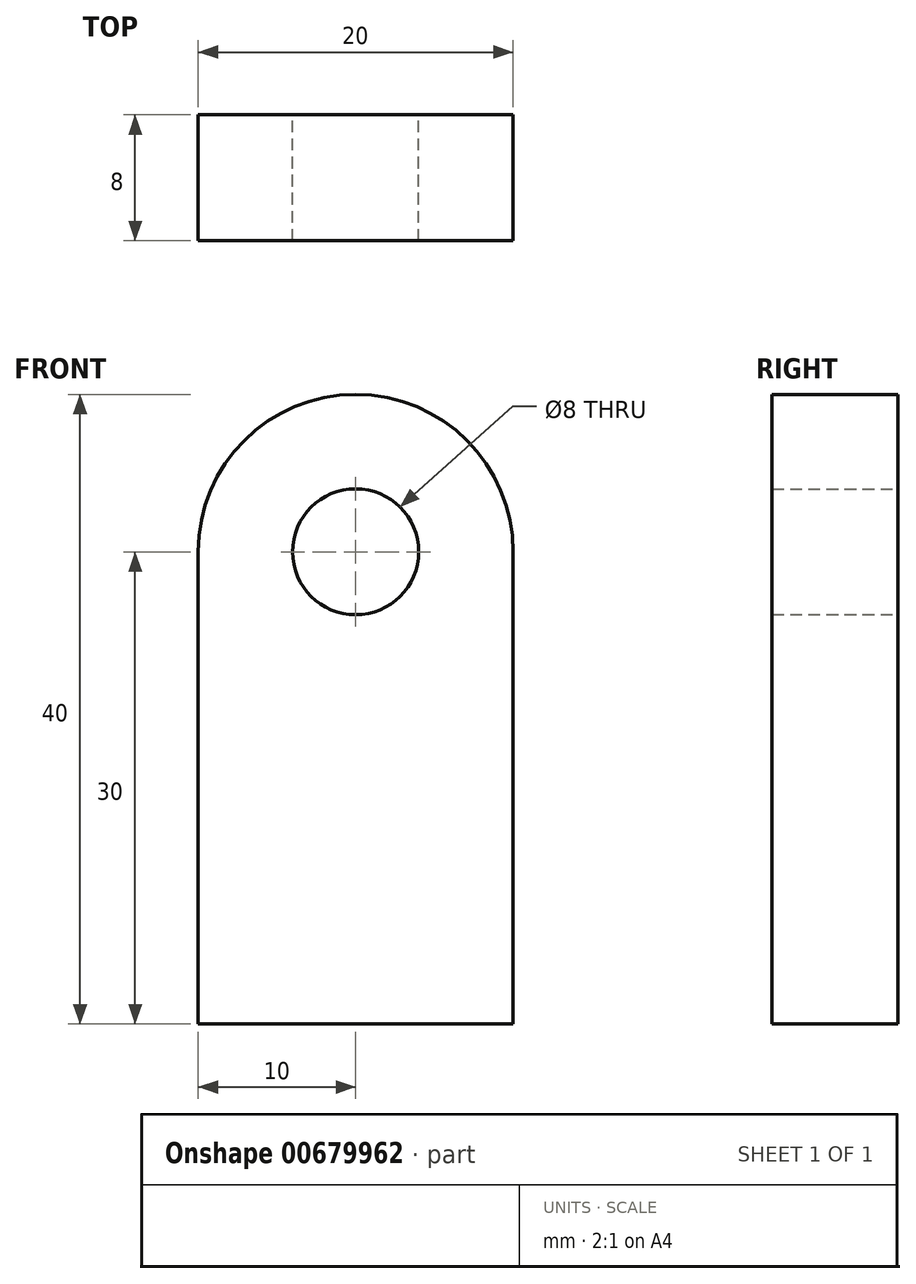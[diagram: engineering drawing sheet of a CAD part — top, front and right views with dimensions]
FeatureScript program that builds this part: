
annotation { "Feature Type Name" : "Feature", "Feature Type Description" : "" }
export const myFeature = defineFeature(function(context is Context, id is Id, definition is map)
    precondition{}
    {
        {
            var Q0;
            Q0=qCreatedBy(makeId("Front.planeOp"),FACE);
            var sketch = newSketch(context, id + "F0", { "sketchPlane" : qUnion([Q0])});
            skCircle(sketch, "E0", {"center": v(0, 30) * mm, "radius": 4 * mm});
            skArc(sketch, "E1", {"start": v(10, 30) * mm, "mid": v(0, 40) * mm, "end": v(-10, 30) * mm});
            skLineSegment(sketch, "E2", {"start": v(-10, 30) * mm, "end": v(-10, 0) * mm});
            skLineSegment(sketch, "E3", {"start": v(10, 30) * mm, "end": v(10, 0) * mm});
            skLineSegment(sketch, "E4", {"start": v(10, 0) * mm, "end": v(-10, 0) * mm});
            skSolve(sketch);
        }
        {
            var Q0;
            Q0 = qSketchRegion(id + "F0", true);
            extrude(context, id + "F1", {"entities" : qUnion([Q0]), "depth" : 8 * mm, "offsetDistance" : 25.4 * mm});
        }
    });
